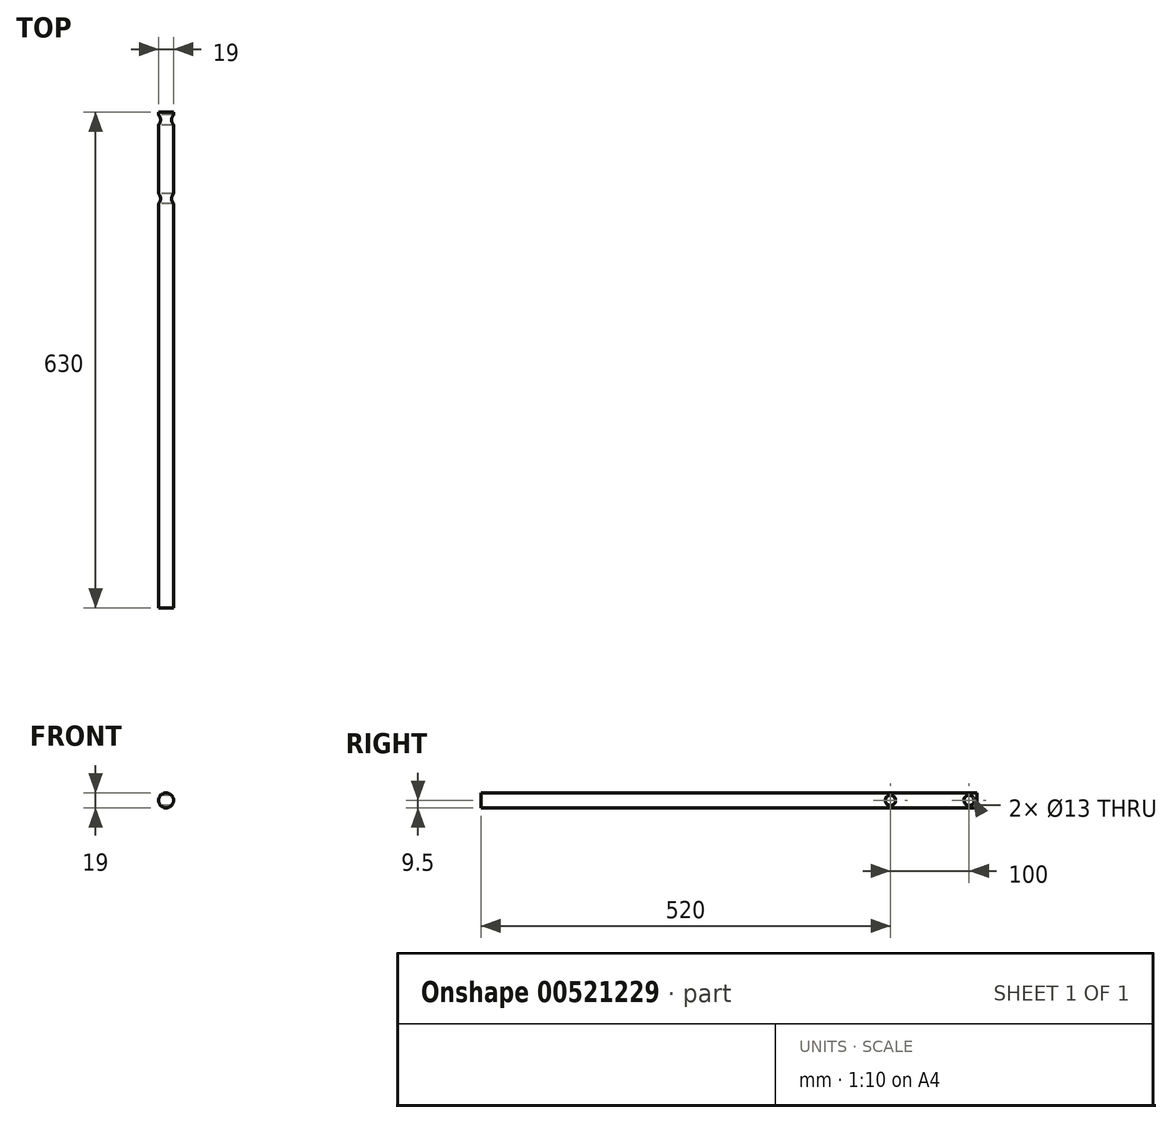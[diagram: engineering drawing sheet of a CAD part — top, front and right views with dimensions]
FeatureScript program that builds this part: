
annotation { "Feature Type Name" : "Feature", "Feature Type Description" : "" }
export const myFeature = defineFeature(function(context is Context, id is Id, definition is map)
    precondition{}
    {
        {
            var Q0;
            Q0=qCreatedBy(makeId("Front.planeOp"),FACE);
            var sketch = newSketch(context, id + "F0", { "sketchPlane" : qUnion([Q0])});
            skCircle(sketch, "E0", {"center": v(0, 0) * mm, "radius": 9.5 * mm});
            skSolve(sketch);
        }
        {
            var Q0;
            Q0=qSketchRegion(id+"F0",true);
            extrude(context, id + "F1", {"entities" : qUnion([Q0]), "depth" : 630 * mm});
        }
        {
            var Q0;
            Q0=qCreatedBy(makeId("Right.planeOp"),FACE);
            var sketch = newSketch(context, id + "F2", { "sketchPlane" : qUnion([Q0])});
            skCircle(sketch, "E1", {"center": v(-10, 0) * mm, "radius": 6.5 * mm});
            skCircle(sketch, "E2", {"center": v(-110, 0) * mm, "radius": 6.5 * mm});
            skSolve(sketch);
        }
        {
            var Q0;
            Q0=qSketchRegion(id+"F2",true);
            extrude(context, id + "F3", {"entities" : qUnion([Q0]), "operationType" : NewBodyOperationType.REMOVE, "depth" : 25 * mm, "hasSecondDirection" : true, "secondDirectionOppositeDirection" : true, "secondDirectionDepth" : 25 * mm});
        }
    });
